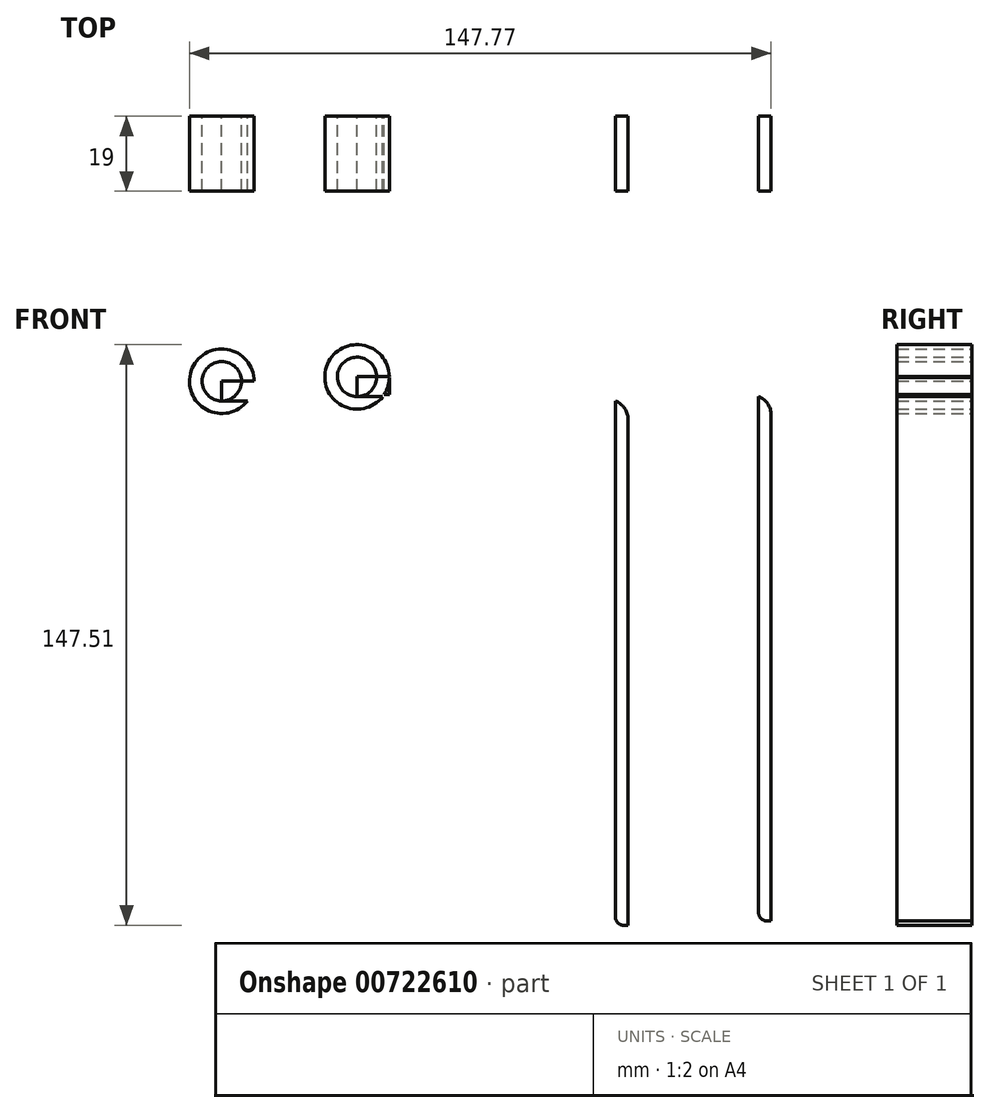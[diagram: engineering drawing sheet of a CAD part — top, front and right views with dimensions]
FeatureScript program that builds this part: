
annotation { "Feature Type Name" : "Feature", "Feature Type Description" : "" }
export const myFeature = defineFeature(function(context is Context, id is Id, definition is map)
    precondition{}
    {
        {
            var Q0;
            Q0=qCreatedBy(makeId("Front.planeOp"),FACE);
            var sketch = newSketch(context, id + "F0", { "sketchPlane" : qUnion([Q0])});
            skLineSegment(sketch, "E0.bottom", {"start": v(-50, 1.6) * mm, "end": v(50, 1.6) * mm});
            skLineSegment(sketch, "E0.top", {"start": v(-50, -1.6) * mm, "end": v(50, -1.6) * mm});
            skLineSegment(sketch, "E0.left", {"start": v(-50, 1.6) * mm, "end": v(-50, -1.6) * mm});
            skLineSegment(sketch, "E0.right", {"start": v(50, 1.6) * mm, "end": v(50, -1.6) * mm});
            skPoint(sketch, "E0.middle", {"position": v(0, 0) * mm});
            skPoint(sketch, "E1", {"position": v(-50, 6.6) * mm});
            skCircle(sketch, "E2", {"center": v(-50, 6.6) * mm, "radius": 5 * mm});
            skCircle(sketch, "E3", {"center": v(-50, 6.6) * mm, "radius": 8.2 * mm});
            skLineSegment(sketch, "E4.bottom", {"start": v(-50, 6.6) * mm, "end": v(-41.8, 6.6) * mm});
            skLineSegment(sketch, "E4.top", {"start": v(-50, 1.6) * mm, "end": v(-41.8, 1.6) * mm});
            skLineSegment(sketch, "E4.left", {"start": v(-50, 6.6) * mm, "end": v(-50, 1.6) * mm});
            skLineSegment(sketch, "E4.right", {"start": v(-41.8, 6.6) * mm, "end": v(-41.8, 1.6) * mm});
            skLineSegment(sketch, "E5.bottom", {"start": v(-50, 1.6) * mm, "end": v(-45, 1.6) * mm});
            skLineSegment(sketch, "E5.top", {"start": v(-50, 6.6) * mm, "end": v(-45, 6.6) * mm});
            skLineSegment(sketch, "E5.left", {"start": v(-50, 1.6) * mm, "end": v(-50, 6.6) * mm});
            skLineSegment(sketch, "E5.right", {"start": v(-45, 1.6) * mm, "end": v(-45, 6.6) * mm});
            skLineSegment(sketch, "E6.bottom", {"start": v(-45, 1.6) * mm, "end": v(-41.8, 1.6) * mm});
            skLineSegment(sketch, "E6.top", {"start": v(-45, 2.1) * mm, "end": v(-41.8, 2.1) * mm});
            skLineSegment(sketch, "E6.left", {"start": v(-45, 1.6) * mm, "end": v(-45, 2.1) * mm});
            skLineSegment(sketch, "E6.right", {"start": v(-41.8, 1.6) * mm, "end": v(-41.8, 2.1) * mm});
            skLineSegment(sketch, "E7.bottom", {"start": v(50, 1.6) * mm, "end": v(53.2, 1.6) * mm});
            skLineSegment(sketch, "E7.top", {"start": v(50, -131.6) * mm, "end": v(53.2, -131.6) * mm});
            skLineSegment(sketch, "E7.left", {"start": v(50, 1.6) * mm, "end": v(50, -131.6) * mm});
            skLineSegment(sketch, "E7.right", {"start": v(53.2, 1.6) * mm, "end": v(53.2, -131.6) * mm});
            skSolve(sketch);
        }
        {
            var Q0;
            {var subQ0=sQuery(id+"F0.wireOp",EDGE,"E0.left");Q0=makeQuery(id+"F0.imprint","IMPRINT",FACE,{"disambiguationData":[TD([[makeQuery(id+"F0.imprint","IMPRINT",EDGE,{"derivedFrom":subQ0}),-1.0]])]});}
            var Q1;
            {var subQ0=sQuery(id+"F0.wireOp",EDGE,"E4.bottom");Q1=makeQuery(id+"F0.imprint","IMPRINT",FACE,{"disambiguationData":[TD([[makeQuery(id+"F0.imprint","IMPRINT",EDGE,{"derivedFrom":subQ0}),-1.0]])]});}
            var Q2;
            {var subQ1=sQuery(id+"F0.wireOp",EDGE,"E0.bottom");Q2=makeQuery(id+"F0.imprint","IMPRINT",FACE,{"disambiguationData":[TD([[makeQuery(id+"F0.imprint","IMPRINT",EDGE,{"derivedFrom":subQ1}),-1.0]])]});}
            var Q3;
            {var subQ0=sQuery(id+"F0.wireOp",EDGE,"E0.left");Q3=makeQuery(id+"F0.imprint","IMPRINT",FACE,{"disambiguationData":[TD([[makeQuery(id+"F0.imprint","IMPRINT",EDGE,{"derivedFrom":subQ0}),1.0]])]});}
            var Q4;
            {var subQ0=sQuery(id+"F0.wireOp",EDGE,"E4.right");Q4=makeQuery(id+"F0.imprint","IMPRINT",FACE,{"disambiguationData":[TD([[makeQuery(id+"F0.imprint","IMPRINT",EDGE,{"derivedFrom":subQ0}),-1.0]])]});}
            var Q5;
            {var subQ3=sQuery(id+"F0.wireOp",EDGE,"E7.bottom");Q5=makeQuery(id+"F0.imprint","IMPRINT",FACE,{"disambiguationData":[TD([[makeQuery(id+"F0.imprint","IMPRINT",EDGE,{"derivedFrom":subQ3}),-1.0]])]});}
            extrude(context, id + "F1", {"entities" : qUnion([Q0, Q1, Q2, Q3, Q4, Q5]), "depth" : 19 * mm, "offsetDistance" : 25 * mm});
        }
        {
            var Q0;
            Q0=makeQuery(id+"F1.opExtrude","SWEPT_EDGE",EDGE,{"disambiguationData":[OSD([sQuery(id+"F0.wireOp",EDGE,"E7.bottom"),sQuery(id+"F0.wireOp",EDGE,"E7.right")])]});
            fillet(context, id + "F2", {"entities" : qUnion([Q0]), "radius" : 5 * mm, "tangentPropagation" : true, "allowEdgeOverflow" : false});
        }
        {
            var Q0;
            Q0=makeQuery(id+"F1.opExtrude","SWEPT_EDGE",EDGE,{"disambiguationData":[OSD([sQuery(id+"F0.wireOp",EDGE,"E0.top"),sQuery(id+"F0.wireOp",EDGE,"E7.left")])]});
            fillet(context, id + "F3", {"entities" : qUnion([Q0]), "radius" : 2 * mm, "tangentPropagation" : true, "allowEdgeOverflow" : false});
        }
        {
            var Q0;
            Q0=makeQuery(id+"F1.opExtrude","CAP_FACE",FACE,{"disambiguationData":[OSD([sQuery(id+"F0.wireOp",EDGE,"E0.bottom"),sQuery(id+"F0.wireOp",EDGE,"E0.top"),sQuery(id+"F0.wireOp",EDGE,"E2"),sQuery(id+"F0.wireOp",EDGE,"E3"),sQuery(id+"F0.wireOp",EDGE,"E4.right"),sQuery(id+"F0.wireOp",EDGE,"E5.bottom"),sQuery(id+"F0.wireOp",EDGE,"E5.right"),sQuery(id+"F0.wireOp",EDGE,"E6.bottom"),sQuery(id+"F0.wireOp",EDGE,"E6.top"),sQuery(id+"F0.wireOp",EDGE,"E7.bottom"),sQuery(id+"F0.wireOp",EDGE,"E7.top"),sQuery(id+"F0.wireOp",EDGE,"E7.left"),sQuery(id+"F0.wireOp",EDGE,"E7.right")])],"isStart":false});
            extrude(context, id + "F4", {"entities" : qUnion([Q0]), "operationType" : NewBodyOperationType.REMOVE, "oppositeDirection" : true, "depth" : 18 * mm, "offsetDistance" : 25 * mm});
        }
        {
            var Q0;
            Q0=makeQuery(id+"F4.boolean.opBoolean","COPY",FACE,{"derivedFrom":makeQuery(id+"F4.opExtrude","CAP_FACE",FACE,{"disambiguationData":[OSD([sQuery(id+"F0.wireOp",EDGE,"E0.bottom"),sQuery(id+"F0.wireOp",EDGE,"E0.top"),sQuery(id+"F0.wireOp",EDGE,"E2"),sQuery(id+"F0.wireOp",EDGE,"E3"),sQuery(id+"F0.wireOp",EDGE,"E4.right"),sQuery(id+"F0.wireOp",EDGE,"E5.bottom"),sQuery(id+"F0.wireOp",EDGE,"E5.right"),sQuery(id+"F0.wireOp",EDGE,"E6.bottom"),sQuery(id+"F0.wireOp",EDGE,"E6.top"),sQuery(id+"F0.wireOp",EDGE,"E7.bottom"),sQuery(id+"F0.wireOp",EDGE,"E7.top"),sQuery(id+"F0.wireOp",EDGE,"E7.left"),sQuery(id+"F0.wireOp",EDGE,"E7.right")])],"isStart":false})});
            extrude(context, id + "F5", {"entities" : qUnion([Q0]), "operationType" : NewBodyOperationType.REMOVE, "oppositeDirection" : true, "depth" : 1 * mm, "offsetDistance" : 25 * mm});
        }
        {
            var Q0;
            Q0=qCreatedBy(makeId("Front.planeOp"),FACE);
            var sketch = newSketch(context, id + "F6", { "sketchPlane" : qUnion([Q0])});
            skLineSegment(sketch, "E8.bottom", {"start": v(-15.63, 2.7) * mm, "end": v(86.37, 2.7) * mm});
            skLineSegment(sketch, "E8.top", {"start": v(-15.63, -0.5) * mm, "end": v(86.37, -0.5) * mm});
            skLineSegment(sketch, "E8.left", {"start": v(-15.63, 2.7) * mm, "end": v(-15.63, -0.5) * mm});
            skLineSegment(sketch, "E8.right", {"start": v(86.37, 2.7) * mm, "end": v(86.37, -0.5) * mm});
            skLineSegment(sketch, "E9.bottom", {"start": v(-15.63, 2.7) * mm, "end": v(-15.63, 2.7) * mm});
            skLineSegment(sketch, "E9.top", {"start": v(-15.63, -0.5) * mm, "end": v(-15.63, -0.5) * mm});
            skPoint(sketch, "E10", {"position": v(-15.63, 2.7) * mm});
            skPoint(sketch, "E11", {"position": v(-15.63, 7.7) * mm});
            skCircle(sketch, "E12", {"center": v(-15.63, 7.7) * mm, "radius": 5 * mm});
            skCircle(sketch, "E13", {"center": v(-15.63, 7.7) * mm, "radius": 8.2 * mm});
            skLineSegment(sketch, "E14.bottom", {"start": v(-15.63, 2.7) * mm, "end": v(-7.43, 2.7) * mm});
            skLineSegment(sketch, "E14.top", {"start": v(-15.63, 7.84) * mm, "end": v(-7.43, 7.84) * mm});
            skLineSegment(sketch, "E14.left", {"start": v(-15.63, 2.7) * mm, "end": v(-15.63, 7.84) * mm});
            skLineSegment(sketch, "E14.right", {"start": v(-7.43, 2.7) * mm, "end": v(-7.43, 7.84) * mm});
            skLineSegment(sketch, "E15.bottom", {"start": v(-15.63, 2.7) * mm, "end": v(-10.63, 2.7) * mm});
            skLineSegment(sketch, "E15.top", {"start": v(-15.63, 7.84) * mm, "end": v(-10.63, 7.84) * mm});
            skLineSegment(sketch, "E15.right", {"start": v(-10.63, 2.7) * mm, "end": v(-10.63, 7.84) * mm});
            skLineSegment(sketch, "E16.bottom", {"start": v(-7.43, 2.7) * mm, "end": v(-10.63, 2.7) * mm});
            skLineSegment(sketch, "E16.top", {"start": v(-7.43, 3.2) * mm, "end": v(-10.63, 3.2) * mm});
            skLineSegment(sketch, "E16.left", {"start": v(-7.43, 2.7) * mm, "end": v(-7.43, 3.2) * mm});
            skLineSegment(sketch, "E16.right", {"start": v(-10.63, 2.7) * mm, "end": v(-10.63, 3.2) * mm});
            skLineSegment(sketch, "E17.bottom", {"start": v(86.37, 2.7) * mm, "end": v(89.57, 2.7) * mm});
            skLineSegment(sketch, "E17.top", {"start": v(86.37, -130.5) * mm, "end": v(89.57, -130.5) * mm});
            skLineSegment(sketch, "E17.left", {"start": v(86.37, 2.7) * mm, "end": v(86.37, -130.5) * mm});
            skLineSegment(sketch, "E17.right", {"start": v(89.57, 2.7) * mm, "end": v(89.57, -130.5) * mm});
            skSolve(sketch);
        }
        {
            var Q0;
            {var subQ0=sQuery(id+"F6.wireOp",EDGE,"E14.right");var subQ1=sQuery(id+"F6.wireOp",EDGE,"E13");var subQ2=makeQuery(id+"F6.imprint","INTERSECT",VERTEX,{"derivedFrom":[subQ1,subQ0]});Q0=makeQuery(id+"F6.imprint","IMPRINT",FACE,{"disambiguationData":[TD([[makeQuery(id+"F6.imprint","IMPRINT",EDGE,{"disambiguationData":[TD([[subQ2,1.0]])],"derivedFrom":subQ1}),-1.0]])]});}
            var Q1;
            {var subQ1=sQuery(id+"F6.wireOp",EDGE,"E14.top");Q1=makeQuery(id+"F6.imprint","IMPRINT",FACE,{"disambiguationData":[TD([[makeQuery(id+"F6.imprint","IMPRINT",EDGE,{"derivedFrom":subQ1}),-1.0]])]});}
            var Q2;
            {var subQ0=sQuery(id+"F6.wireOp",EDGE,"E8.left");Q2=makeQuery(id+"F6.imprint","IMPRINT",FACE,{"disambiguationData":[TD([[makeQuery(id+"F6.imprint","IMPRINT",EDGE,{"derivedFrom":subQ0}),-1.0]])]});}
            var Q3;
            {var subQ1=sQuery(id+"F6.wireOp",EDGE,"E8.bottom");Q3=makeQuery(id+"F6.imprint","IMPRINT",FACE,{"disambiguationData":[TD([[makeQuery(id+"F6.imprint","IMPRINT",EDGE,{"derivedFrom":subQ1}),-1.0]])]});}
            var Q4;
            {var subQ0=sQuery(id+"F6.wireOp",EDGE,"E8.left");Q4=makeQuery(id+"F6.imprint","IMPRINT",FACE,{"disambiguationData":[TD([[makeQuery(id+"F6.imprint","IMPRINT",EDGE,{"derivedFrom":subQ0}),1.0]])]});}
            var Q5;
            {var subQ3=sQuery(id+"F6.wireOp",EDGE,"E17.bottom");Q5=makeQuery(id+"F6.imprint","IMPRINT",FACE,{"disambiguationData":[TD([[makeQuery(id+"F6.imprint","IMPRINT",EDGE,{"derivedFrom":subQ3}),-1.0]])]});}
            extrude(context, id + "F7", {"entities" : qUnion([Q0, Q1, Q2, Q3, Q4, Q5]), "depth" : 19 * mm, "offsetDistance" : 25 * mm});
        }
        {
            var Q0;
            Q0=makeQuery(id+"F7.opExtrude","SWEPT_EDGE",EDGE,{"disambiguationData":[OSD([sQuery(id+"F6.wireOp",EDGE,"E17.bottom"),sQuery(id+"F6.wireOp",EDGE,"E17.right")])]});
            fillet(context, id + "F8", {"entities" : qUnion([Q0]), "radius" : 5 * mm, "tangentPropagation" : true, "allowEdgeOverflow" : false});
        }
        {
            var Q0;
            Q0=makeQuery(id+"F7.opExtrude","SWEPT_EDGE",EDGE,{"disambiguationData":[OSD([sQuery(id+"F6.wireOp",EDGE,"E8.top"),sQuery(id+"F6.wireOp",EDGE,"E17.left")])]});
            fillet(context, id + "F9", {"entities" : qUnion([Q0]), "radius" : 2 * mm, "tangentPropagation" : true, "allowEdgeOverflow" : false});
        }
    });
